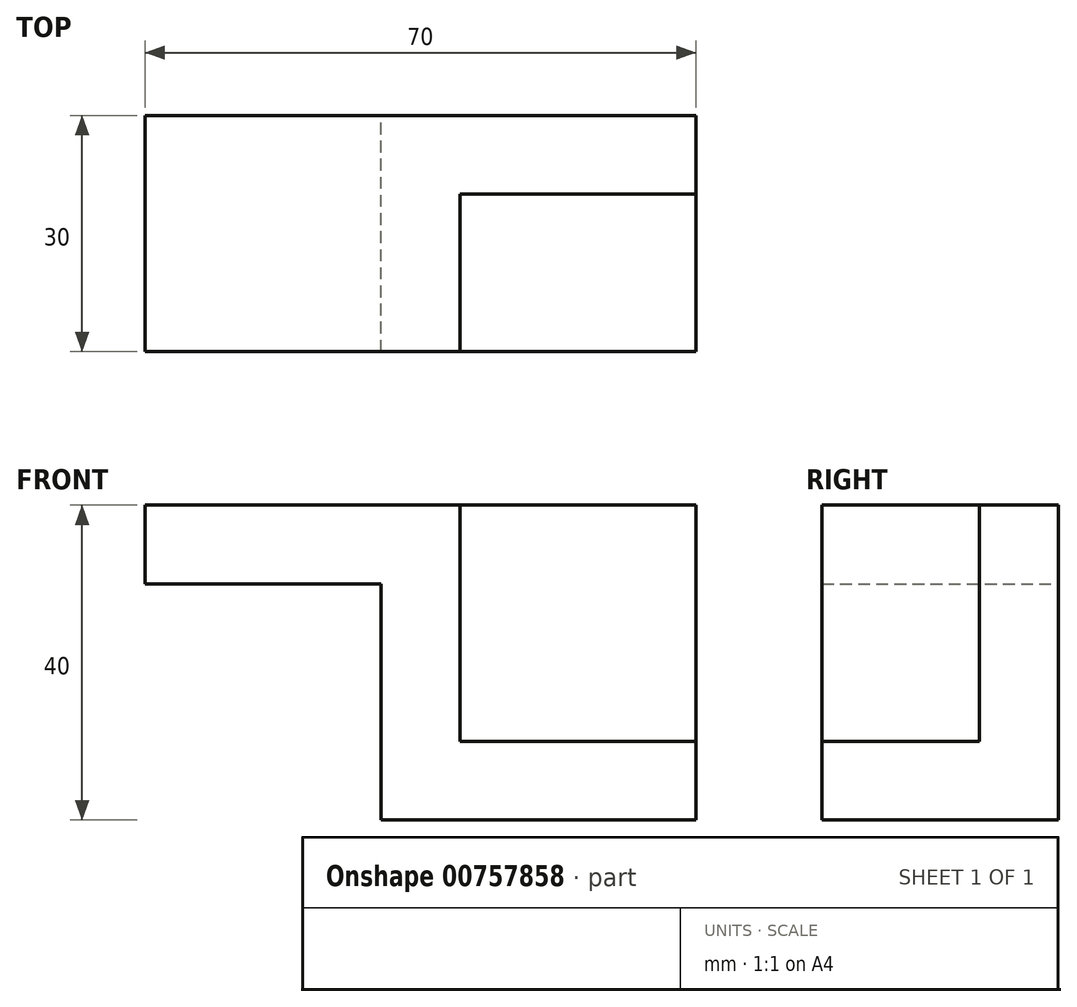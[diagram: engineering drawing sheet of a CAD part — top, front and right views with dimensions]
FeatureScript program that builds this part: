
annotation { "Feature Type Name" : "Feature", "Feature Type Description" : "" }
export const myFeature = defineFeature(function(context is Context, id is Id, definition is map)
    precondition{}
    {
        {
            var Q0;
            Q0=qCreatedBy(makeId("Front.planeOp"),FACE);
            var sketch = newSketch(context, id + "F0", { "sketchPlane" : qUnion([Q0])});
            skLineSegment(sketch, "E0", {"start": v(0, 0) * mm, "end": v(-40, 0) * mm});
            skLineSegment(sketch, "E1", {"start": v(-40, 0) * mm, "end": v(-40, 30) * mm});
            skLineSegment(sketch, "E2", {"start": v(-40, 30) * mm, "end": v(-70, 30) * mm});
            skLineSegment(sketch, "E3", {"start": v(-70, 30) * mm, "end": v(-70, 40) * mm});
            skLineSegment(sketch, "E4", {"start": v(-70, 40) * mm, "end": v(0, 40) * mm});
            skLineSegment(sketch, "E5", {"start": v(0, 40) * mm, "end": v(0, 0) * mm});
            skSolve(sketch);
        }
        {
            var Q0;
            Q0 = qSketchRegion(id + "F0", true);
            extrude(context, id + "F1", {"entities" : qUnion([Q0]), "depth" : 30 * mm, "offsetDistance" : 25 * mm});
        }
        {
            var Q0;
            Q0=makeQuery(id+"F1.opExtrude","CAP_FACE",FACE,{"disambiguationData":[OSD([sQuery(id+"F0.wireOp",EDGE,"E0"),sQuery(id+"F0.wireOp",EDGE,"E1"),sQuery(id+"F0.wireOp",EDGE,"E2"),sQuery(id+"F0.wireOp",EDGE,"E3"),sQuery(id+"F0.wireOp",EDGE,"E4"),sQuery(id+"F0.wireOp",EDGE,"E5")])],"isStart":false});
            var sketch = newSketch(context, id + "F2", { "sketchPlane" : qUnion([Q0])});
            skLineSegment(sketch, "E6", {"start": v(-30, 40) * mm, "end": v(-30, 10) * mm});
            skLineSegment(sketch, "E7", {"start": v(-30, 10) * mm, "end": v(0, 10) * mm});
            skSolve(sketch);
        }
        {
            var Q0;
            {var subQ0=sQuery(id+"F2.wireOp",EDGE,"E6");Q0=makeQuery(id+"F2.imprint","IMPRINT",FACE,{"disambiguationData":[TD([[makeQuery(id+"F2.imprint","IMPRINT",EDGE,{"derivedFrom":subQ0}),1.0]])]});}
            extrude(context, id + "F3", {"entities" : qUnion([Q0]), "operationType" : NewBodyOperationType.REMOVE, "oppositeDirection" : true, "depth" : 20 * mm, "offsetDistance" : 25 * mm});
        }
    });
